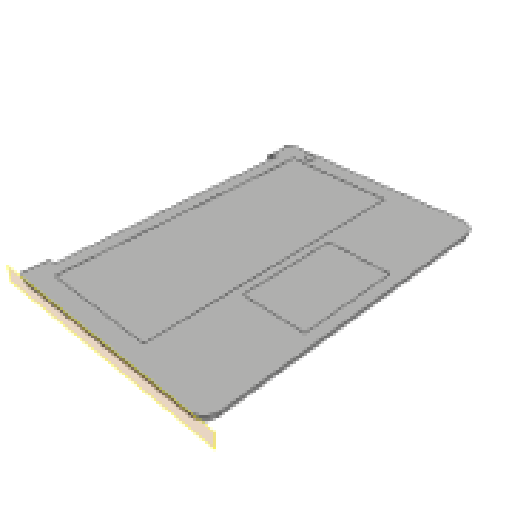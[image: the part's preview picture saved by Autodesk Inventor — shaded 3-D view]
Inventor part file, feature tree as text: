
AUTODESK INVENTOR PART (.ipt)
format: ipt  version: 2025 (Build 290162000, 162)  size: 233,472 bytes
history: native  units: mm
features: extrude x6, sketch x6, projected_geometry x6, fillet x1, plane x1, mirror x1
ambient origin geometry x8: Origin, YZ Plane, XZ Plane, XY Plane, X Axis, Y Axis, Z Axis, Center Point
bodies: Solid1 (feature_tree)
feature tree (21):
  extrude  "Extrusion1"  Depth=234.95mm
  extrude  "Extrusion2"  Depth=15.875mm TaperAngle=0.0deg
  fillet  "Fillet1"  Radius=20.6375mm
  extrude  "Extrusion3"  Depth=29.21mm
  extrude  "Extrusion4"  Depth=104.775mm
  extrude  "Extrusion5"  Depth=9.525mm
  plane  "Work Plane2"
  extrude  "Extrusion6"  Depth=15.875mm
  mirror  "Mirror2"
  sketch  "Sketch1"  dims[d0=330.2mm d1=234.95mm]
  sketch  "Sketch2"  dims[d2=15.875mm d3=15.3035mm d4=0.0mm d5=20.6375mm]
  projected_geometry  "Projected Loop1"
  sketch  "Sketch3"  dims[d6=20.6375mm d7=29.21mm]
  projected_geometry  "Projected Loop2"
  sketch  "Sketch4"  dims[d8=117.1575mm d9=104.775mm]
  projected_geometry  "Projected Loop3"
  sketch  "Sketch5"  dims[d10=66.04mm d11=9.525mm]
  projected_geometry  "Projected Loop4"
  sketch  "Sketch6"  dims[d12=0.254mm d13=0.0mm d14=15.875mm d15=31.75mm d16=31.75mm d17=13.97mm d18=0.0mm d19=0.0mm d20=300.0mm d21=0.0mm d22=0.0mm d23=0.0mm d24=114.3mm d25=10.0mm d26=0.0mm]
  projected_geometry  "Projected Loop5"
  projected_geometry  "Projected Loop6"
